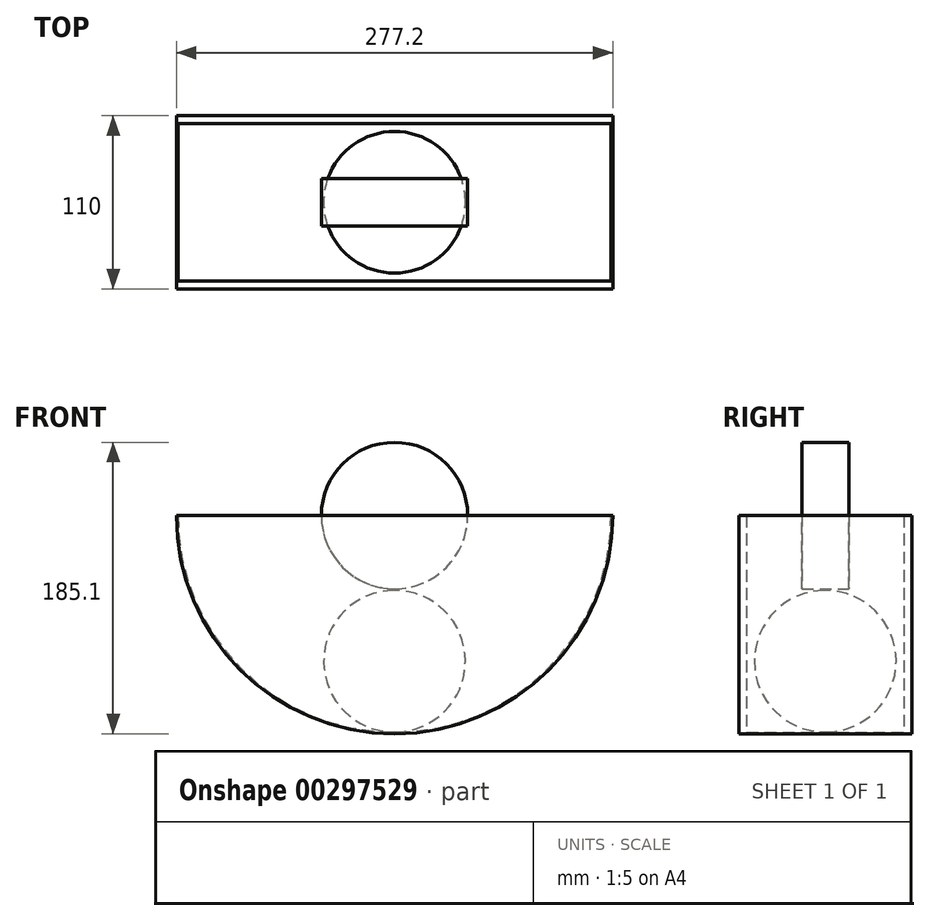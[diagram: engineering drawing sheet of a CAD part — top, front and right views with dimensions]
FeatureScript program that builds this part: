
annotation { "Feature Type Name" : "Feature", "Feature Type Description" : "" }
export const myFeature = defineFeature(function(context is Context, id is Id, definition is map)
    precondition{}
    {
        {
            var Q0;
            Q0=qCreatedBy(makeId("Front.planeOp"),FACE);
            var sketch = newSketch(context, id + "F0", { "sketchPlane" : qUnion([Q0])});
            skCircle(sketch, "E0", {"center": v(0, 0) * mm, "radius": 46.5 * mm});
            skSolve(sketch);
        }
        {
            var Q0;
            Q0 = qSketchRegion(id + "F0", true);
            extrude(context, id + "F1", {"entities" : qUnion([Q0]), "endBound" : BoundingType.SYMMETRIC, "depth" : 30 * mm});
        }
        {
            var Q0;
            Q0=qCreatedBy(makeId("Front.planeOp"),FACE);
            var sketch = newSketch(context, id + "F2", { "sketchPlane" : qUnion([Q0])});
            skCircle(sketch, "E1", {"center": v(0, -92.5) * mm, "radius": 45 * mm});
            skLineSegment(sketch, "E2", {"start": v(0, -47.5) * mm, "end": v(0, -137.5) * mm});
            skCircle(sketch, "E3", {"center": v(0, 0) * mm, "radius": 137.6 * mm});
            skCircle(sketch, "E4", {"center": v(0, 0) * mm, "radius": 138.6 * mm});
            skLineSegment(sketch, "E5", {"start": v(0, 0) * mm, "end": v(-138.6, 0) * mm});
            skLineSegment(sketch, "E6", {"start": v(0, 0) * mm, "end": v(138.6, 0) * mm});
            skSolve(sketch);
        }
        {
            var Q0;
            {var subQ0=sQuery(id+"F2.wireOp",EDGE,"E2");Q0=makeQuery(id+"F2.imprint","IMPRINT",FACE,{"disambiguationData":[TD([[makeQuery(id+"F2.imprint","IMPRINT",EDGE,{"derivedFrom":subQ0}),-1.0]])]});}
            var Q1;
            Q1=sQuery(id+"F2.wireOp",EDGE,"E2");
            revolve(context, id + "F3", {"entities" : qUnion([Q0]), "axis" : qUnion([Q1]), "revolveType" : RevolveType.FULL});
        }
        {
            var Q0;
            {var subQ0=sQuery(id+"F2.wireOp",EDGE,"E5");var subQ1=sQuery(id+"F2.wireOp",EDGE,"E3");var subQ2=makeQuery(id+"F2.imprint","INTERSECT",VERTEX,{"derivedFrom":[subQ1,subQ0]});Q0=makeQuery(id+"F2.imprint","IMPRINT",FACE,{"disambiguationData":[TD([[makeQuery(id+"F2.imprint","IMPRINT",EDGE,{"disambiguationData":[TD([[subQ2,-1.0]])],"derivedFrom":subQ1}),-1.0]])]});}
            extrude(context, id + "F4", {"entities" : qUnion([Q0]), "endBound" : BoundingType.SYMMETRIC, "depth" : 110 * mm});
        }
        {
            var Q0;
            {var subQ6=sQuery(id+"F2.wireOp",EDGE,"E2");var subQ7=sQuery(id+"F2.wireOp",EDGE,"E1");var subQ8=makeQuery(id+"F2.imprint","INTERSECT",VERTEX,{"disambiguationData":[OD(0.0)],"derivedFrom":[subQ7,subQ6]});Q0=makeQuery(id+"F2.imprint","IMPRINT",FACE,{"disambiguationData":[TD([[makeQuery(id+"F2.imprint","IMPRINT",EDGE,{"disambiguationData":[TD([[subQ8,-1.0]])],"derivedFrom":subQ7}),-1.0]])]});}
            var Q1;
            {var subQ0=sQuery(id+"F2.wireOp",EDGE,"E2");Q1=makeQuery(id+"F2.imprint","IMPRINT",FACE,{"disambiguationData":[TD([[makeQuery(id+"F2.imprint","IMPRINT",EDGE,{"derivedFrom":subQ0}),1.0]])]});}
            var Q2;
            {var subQ0=sQuery(id+"F2.wireOp",EDGE,"E2");Q2=makeQuery(id+"F2.imprint","IMPRINT",FACE,{"disambiguationData":[TD([[makeQuery(id+"F2.imprint","IMPRINT",EDGE,{"derivedFrom":subQ0}),-1.0]])]});}
            extrude(context, id + "F5", {"entities" : qUnion([Q0, Q1, Q2]), "operationType" : NewBodyOperationType.ADD, "depth" : 110 / 2 * mm, "hasSecondDirection" : true, "secondDirectionOppositeDirection" : false, "secondDirectionDepth" : 100 / 2 * mm});
        }
        {
            var Q0;
            {var subQ6=sQuery(id+"F2.wireOp",EDGE,"E2");var subQ7=sQuery(id+"F2.wireOp",EDGE,"E1");var subQ8=makeQuery(id+"F2.imprint","INTERSECT",VERTEX,{"disambiguationData":[OD(0.0)],"derivedFrom":[subQ7,subQ6]});Q0=makeQuery(id+"F2.imprint","IMPRINT",FACE,{"disambiguationData":[TD([[makeQuery(id+"F2.imprint","IMPRINT",EDGE,{"disambiguationData":[TD([[subQ8,-1.0]])],"derivedFrom":subQ7}),-1.0]])]});}
            var Q1;
            {var subQ0=sQuery(id+"F2.wireOp",EDGE,"E2");Q1=makeQuery(id+"F2.imprint","IMPRINT",FACE,{"disambiguationData":[TD([[makeQuery(id+"F2.imprint","IMPRINT",EDGE,{"derivedFrom":subQ0}),1.0]])]});}
            var Q2;
            {var subQ0=sQuery(id+"F2.wireOp",EDGE,"E2");Q2=makeQuery(id+"F2.imprint","IMPRINT",FACE,{"disambiguationData":[TD([[makeQuery(id+"F2.imprint","IMPRINT",EDGE,{"derivedFrom":subQ0}),-1.0]])]});}
            extrude(context, id + "F6", {"entities" : qUnion([Q0, Q1, Q2]), "operationType" : NewBodyOperationType.ADD, "oppositeDirection" : true, "depth" : (110 / 2) * mm, "hasSecondDirection" : true, "secondDirectionOppositeDirection" : true, "secondDirectionDepth" : 50 * mm});
        }
    });
